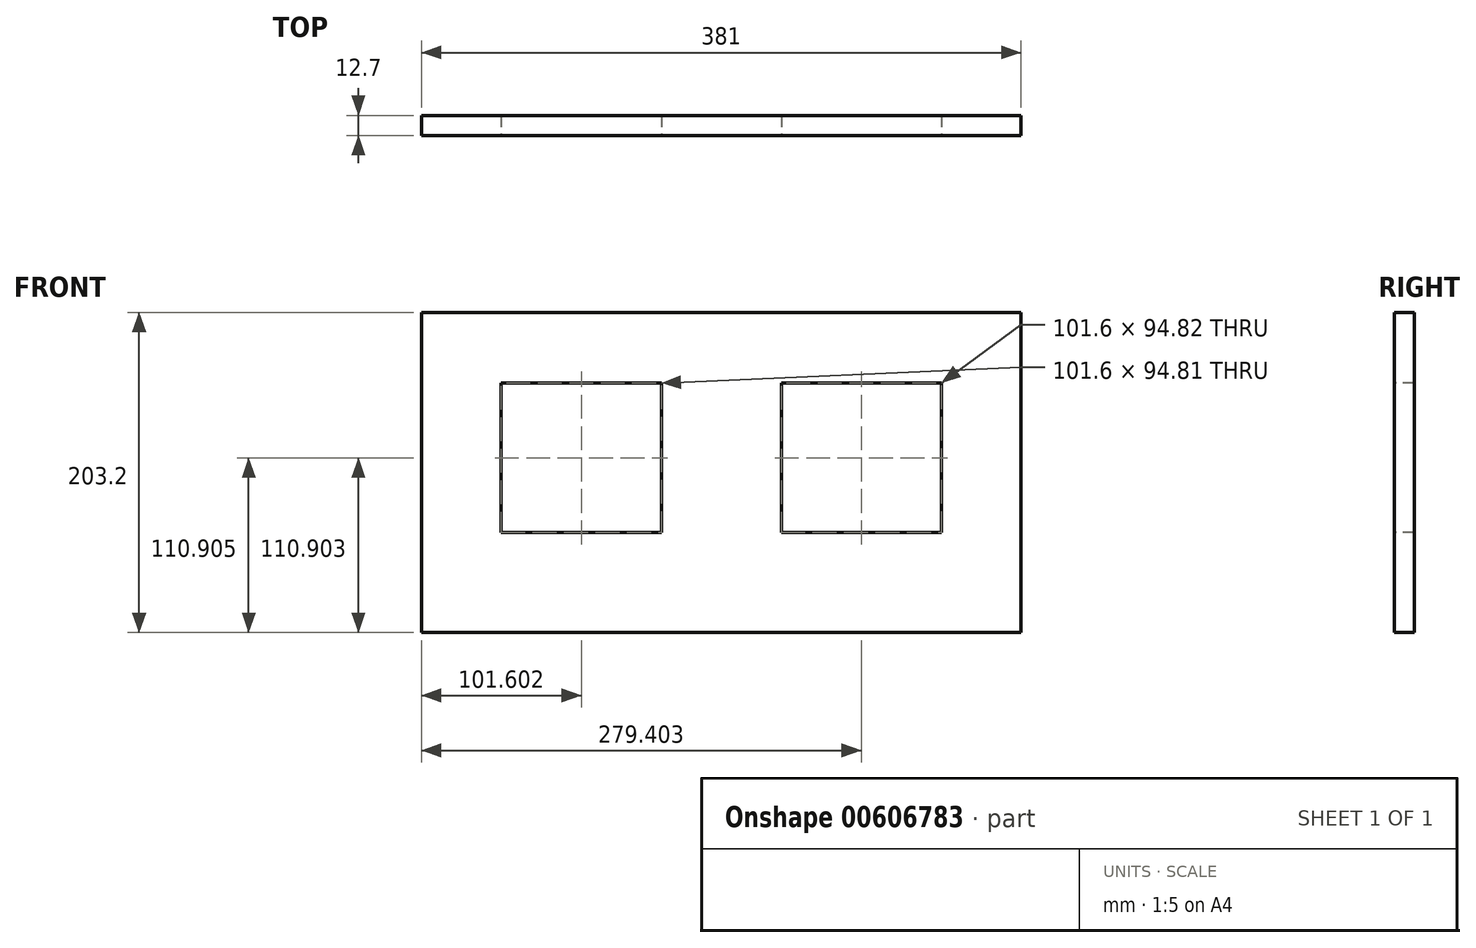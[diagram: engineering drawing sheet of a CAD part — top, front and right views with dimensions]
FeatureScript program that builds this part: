
annotation { "Feature Type Name" : "Feature", "Feature Type Description" : "" }
export const myFeature = defineFeature(function(context is Context, id is Id, definition is map)
    precondition{}
    {
        {
            var Q0;
            Q0=qCreatedBy(makeId("Front.planeOp"),FACE);
            var sketch = newSketch(context, id + "F0", { "sketchPlane" : qUnion([Q0])});
            skLineSegment(sketch, "E0.bottom", {"start": v(-139.04, 96.09) * mm, "end": v(241.96, 96.09) * mm});
            skLineSegment(sketch, "E0.top", {"start": v(-139.04, -107.11) * mm, "end": v(241.96, -107.11) * mm});
            skLineSegment(sketch, "E0.left", {"start": v(-139.04, 96.09) * mm, "end": v(-139.04, -107.11) * mm});
            skLineSegment(sketch, "E0.right", {"start": v(241.96, 96.09) * mm, "end": v(241.96, -107.11) * mm});
            skSolve(sketch);
        }
        {
            var Q0;
            Q0 = qSketchRegion(id + "F0", true);
            extrude(context, id + "F1", {"entities" : qUnion([Q0]), "depth" : 12.7 * mm, "offsetDistance" : 25.4 * mm});
        }
        {
            var Q0;
            Q0=makeQuery(id+"F1.opExtrude","CAP_FACE",FACE,{"disambiguationData":[OSD([sQuery(id+"F0.wireOp",EDGE,"E0.bottom"),sQuery(id+"F0.wireOp",EDGE,"E0.top"),sQuery(id+"F0.wireOp",EDGE,"E0.left"),sQuery(id+"F0.wireOp",EDGE,"E0.right")])],"isStart":false});
            var sketch = newSketch(context, id + "F2", { "sketchPlane" : qUnion([Q0])});
            skSolve(sketch);
        }
        {
            var Q0;
            Q0=makeQuery(id+"F2.imprint","IMPRINT",FACE,{"disambiguationData":[TD([[makeQuery(id+"F2.imprint","IMPRINT",EDGE,{"derivedFrom":makeQuery(id+"F1.opExtrude","CAP_EDGE",EDGE,{"disambiguationData":[OSD([sQuery(id+"F0.wireOp",EDGE,"E0.bottom")])],"isStart":false})}),-1.0]])]});
            var sketch = newSketch(context, id + "F3", { "sketchPlane" : qUnion([Q0])});
            skLineSegment(sketch, "E1.bottom", {"start": v(-88.24, 51.2) * mm, "end": v(13.36, 51.2) * mm});
            skLineSegment(sketch, "E1.top", {"start": v(-88.24, -43.61) * mm, "end": v(13.36, -43.61) * mm});
            skLineSegment(sketch, "E1.left", {"start": v(-88.24, 51.2) * mm, "end": v(-88.24, -43.61) * mm});
            skLineSegment(sketch, "E1.right", {"start": v(13.36, 51.2) * mm, "end": v(13.36, -43.61) * mm});
            skLineSegment(sketch, "E2.bottom", {"start": v(89.56, 51.2) * mm, "end": v(191.16, 51.2) * mm});
            skLineSegment(sketch, "E2.top", {"start": v(89.56, -43.61) * mm, "end": v(191.16, -43.61) * mm});
            skLineSegment(sketch, "E2.left", {"start": v(89.56, 51.2) * mm, "end": v(89.56, -43.61) * mm});
            skLineSegment(sketch, "E2.right", {"start": v(191.16, 51.2) * mm, "end": v(191.16, -43.61) * mm});
            skSolve(sketch);
        }
        {
            var Q0;
            Q0 = qSketchRegion(id + "F3", true);
            extrude(context, id + "F4", {"entities" : qUnion([Q0]), "operationType" : NewBodyOperationType.REMOVE, "endBound" : BoundingType.THROUGH_ALL, "oppositeDirection" : true, "depth" : 25.4 * mm, "offsetDistance" : 25.4 * mm});
        }
    });
